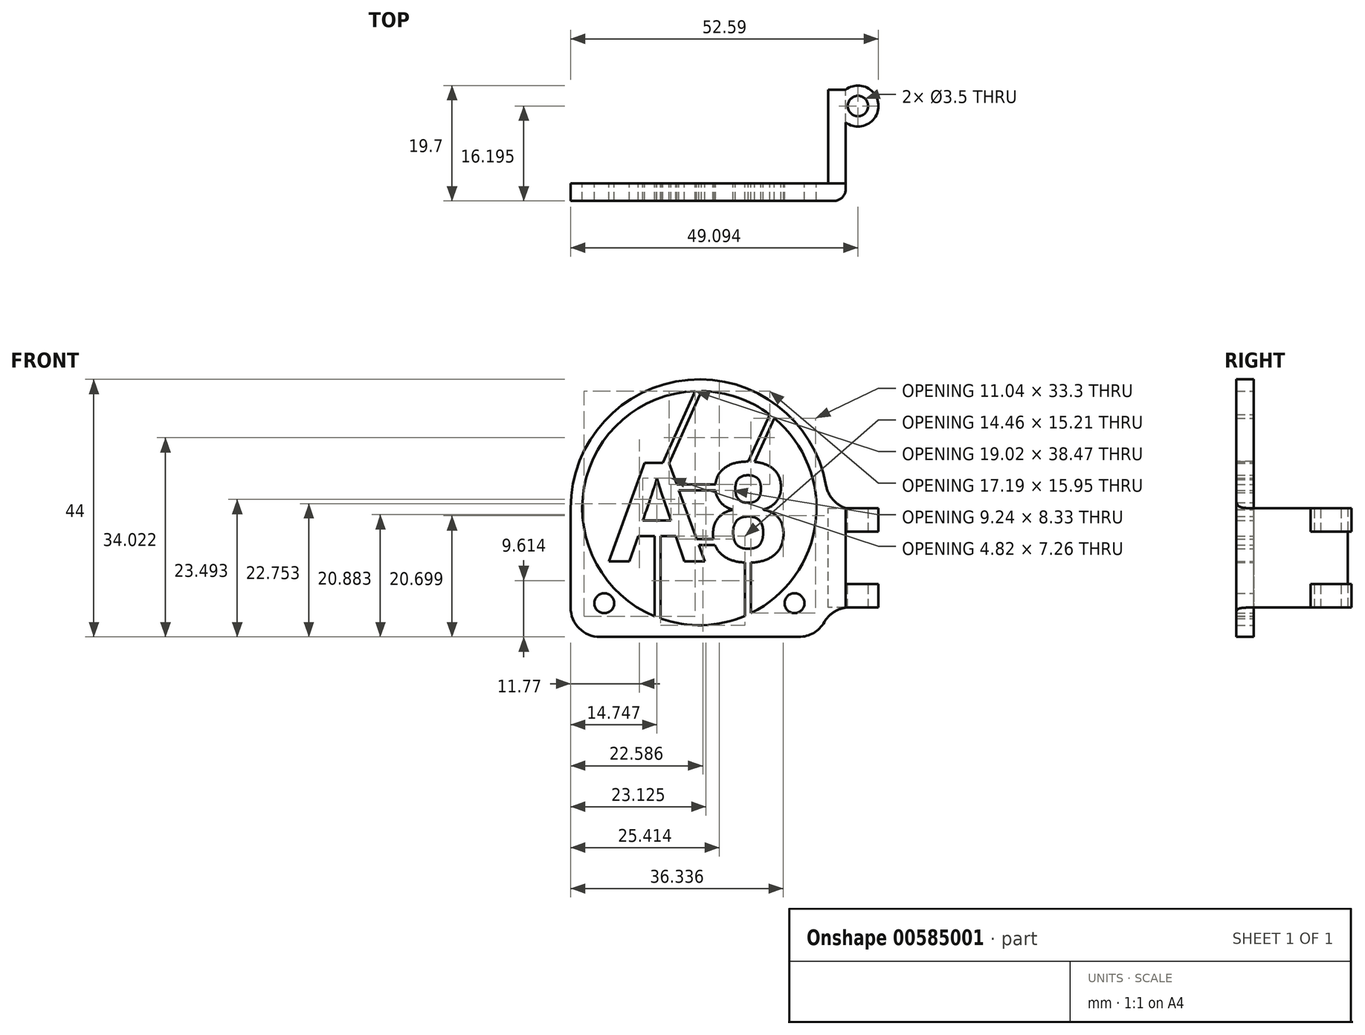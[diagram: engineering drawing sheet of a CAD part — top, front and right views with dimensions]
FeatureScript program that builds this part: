
annotation { "Feature Type Name" : "Feature", "Feature Type Description" : "" }
export const myFeature = defineFeature(function(context is Context, id is Id, definition is map)
    precondition{}
    {
        {
            var Q0;
            Q0=qCreatedBy(makeId("Front.planeOp"),FACE);
            var sketch = newSketch(context, id + "F0", { "sketchPlane" : qUnion([Q0])});
            skPoint(sketch, "E0.middle", {"position": v(0, 0) * mm});
            skCircle(sketch, "E1", {"center": v(-16.25, -16.25) * mm, "radius": 1.7 * mm});
            skCircle(sketch, "E2", {"center": v(16.25, -16.25) * mm, "radius": 1.7 * mm});
            skLineSegment(sketch, "E3.bottom", {"start": v(-17, -22) * mm, "end": v(17, -22) * mm});
            skLineSegment(sketch, "E3.left", {"start": v(-22, -17) * mm, "end": v(-22, 0) * mm});
            skLineSegment(sketch, "E3.right", {"start": v(22, -17) * mm, "end": v(22, 0) * mm});
            skCircle(sketch, "E4", {"center": v(0, 0) * mm, "radius": 20 * mm});
            skArc(sketch, "E5", {"start": v(22, 0) * mm, "mid": v(0, 22) * mm, "end": v(-22, 0) * mm});
            skPoint(sketch, "E6.orphan", {"position": v(-22, 22) * mm});
            skPoint(sketch, "E7.orphan", {"position": v(22, 22) * mm});
            skText(sketch, "E8", { "text": "A8", "fontName": "Arimo-Bold.ttf"});
            skLineSegment(sketch, "E9", {"start": v(-7.64, -3.72) * mm, "end": v(-7.64, -18.48) * mm});
            skLineSegment(sketch, "E10", {"start": v(-6.64, -18.86) * mm, "end": v(-6.64, -3.39) * mm});
            skLineSegment(sketch, "E11", {"start": v(7.81, -18.41) * mm, "end": v(7.81, -7.77) * mm});
            skLineSegment(sketch, "E12", {"start": v(8.81, -17.95) * mm, "end": v(8.81, -7.9) * mm});
            skLineSegment(sketch, "E13", {"start": v(3.64, -5.28) * mm, "end": v(-2.18, -5.28) * mm});
            skLineSegment(sketch, "E14", {"start": v(-2.25, -6.28) * mm, "end": v(3.9, -6.28) * mm});
            skLineSegment(sketch, "E15", {"start": v(3.52, 4.05) * mm, "end": v(-6.25, 4.05) * mm});
            skLineSegment(sketch, "E16", {"start": v(-5.4, 3.05) * mm, "end": v(4.44, 3.05) * mm});
            skLineSegment(sketch, "E17", {"start": v(-0.72, 19.99) * mm, "end": v(-6.99, 6.13) * mm});
            skLineSegment(sketch, "E18", {"start": v(12.01, 16) * mm, "end": v(8.12, 7.4) * mm});
            skLineSegment(sketch, "E19", {"start": v(12.82, 15.35) * mm, "end": v(9.09, 7.1) * mm});
            skLineSegment(sketch, "E20", {"start": v(0.38, 20) * mm, "end": v(-5.47, 7.07) * mm});
            skPoint(sketch, "E21.visualSharp", {"position": v(22, -22) * mm});
            skArc(sketch, "E21.filletArc", {"start": v(17, -22) * mm, "mid": v(20.54, -20.54) * mm, "end": v(22, -17) * mm});
            skPoint(sketch, "E22.visualSharp", {"position": v(-22, -22) * mm});
            skArc(sketch, "E22.filletArc", {"start": v(-22, -17) * mm, "mid": v(-20.54, -20.54) * mm, "end": v(-17, -22) * mm});
            const initialGuessF0  = {"E8": [-0.01606, -0.00907, 1, 0, 0.01756]};
            skSetInitialGuess(sketch, initialGuessF0);
            skSolve(sketch);
        }
        {
            var Q0;
            Q0=makeQuery(id+"F0.imprint","IMPRINT",FACE,{"disambiguationData":[TD([[makeQuery(id+"F0.imprint","IMPRINT",EDGE,{"derivedFrom":sQuery(id+"F0.wireOp",EDGE,"E1")}),-1.0]])]});
            var Q1;
            {var subQ18=sQuery(id+"F0.wireOp",EDGE,"E8.sketch_text.stroke-15");Q1=makeQuery(id+"F0.imprint","IMPRINT",FACE,{"disambiguationData":[TD([[makeQuery(id+"F0.imprint","IMPRINT",EDGE,{"derivedFrom":subQ18}),-1.0]])]});}
            var Q2;
            {var subQ3=sQuery(id+"F0.wireOp",EDGE,"E18");var subQ5=sQuery(id+"F0.wireOp",EDGE,"E4");var subQ6=makeQuery(id+"F0.imprint","INTERSECT",VERTEX,{"derivedFrom":[subQ5,subQ3]});Q2=makeQuery(id+"F0.imprint","IMPRINT",FACE,{"disambiguationData":[TD([[makeQuery(id+"F0.imprint","IMPRINT",EDGE,{"disambiguationData":[TD([[subQ6,1.0]])],"derivedFrom":subQ5}),1.0]])]});}
            var Q3;
            {var subQ0=sQuery(id+"F0.wireOp",EDGE,"E17");var subQ1=sQuery(id+"F0.wireOp",EDGE,"E4");var subQ2=makeQuery(id+"F0.imprint","INTERSECT",VERTEX,{"derivedFrom":[subQ1,subQ0]});Q3=makeQuery(id+"F0.imprint","IMPRINT",FACE,{"disambiguationData":[TD([[makeQuery(id+"F0.imprint","IMPRINT",EDGE,{"disambiguationData":[TD([[subQ2,1.0]])],"derivedFrom":subQ1}),1.0]])]});}
            var Q4;
            {var subQ11=sQuery(id+"F0.wireOp",EDGE,"E8.sketch_text.stroke-0");Q4=makeQuery(id+"F0.imprint","IMPRINT",FACE,{"disambiguationData":[TD([[makeQuery(id+"F0.imprint","IMPRINT",EDGE,{"derivedFrom":subQ11}),-1.0]])]});}
            var Q5;
            {var subQ0=sQuery(id+"F0.wireOp",EDGE,"E15");var subQ1=sQuery(id+"F0.wireOp",EDGE,"E8.sketch_text.stroke-6");var subQ2=makeQuery(id+"F0.imprint","INTERSECT",VERTEX,{"derivedFrom":[subQ1,subQ0]});Q5=makeQuery(id+"F0.imprint","IMPRINT",FACE,{"disambiguationData":[TD([[makeQuery(id+"F0.imprint","IMPRINT",EDGE,{"disambiguationData":[TD([[subQ2,-1.0]])],"derivedFrom":subQ1}),1.0]])]});}
            var Q6;
            {var subQ0=sQuery(id+"F0.wireOp",EDGE,"E13");var subQ1=sQuery(id+"F0.wireOp",EDGE,"E8.sketch_text.stroke-6");var subQ2=makeQuery(id+"F0.imprint","INTERSECT",VERTEX,{"derivedFrom":[subQ1,subQ0]});Q6=makeQuery(id+"F0.imprint","IMPRINT",FACE,{"disambiguationData":[TD([[makeQuery(id+"F0.imprint","IMPRINT",EDGE,{"disambiguationData":[TD([[subQ2,-1.0]])],"derivedFrom":subQ1}),1.0]])]});}
            var Q7;
            {var subQ0=sQuery(id+"F0.wireOp",EDGE,"E9");var subQ1=sQuery(id+"F0.wireOp",EDGE,"E4");var subQ2=makeQuery(id+"F0.imprint","INTERSECT",VERTEX,{"derivedFrom":[subQ1,subQ0]});Q7=makeQuery(id+"F0.imprint","IMPRINT",FACE,{"disambiguationData":[TD([[makeQuery(id+"F0.imprint","IMPRINT",EDGE,{"disambiguationData":[TD([[subQ2,-1.0]])],"derivedFrom":subQ1}),1.0]])]});}
            var Q8;
            {var subQ0=sQuery(id+"F0.wireOp",EDGE,"E11");var subQ1=sQuery(id+"F0.wireOp",EDGE,"E4");var subQ2=makeQuery(id+"F0.imprint","INTERSECT",VERTEX,{"derivedFrom":[subQ1,subQ0]});Q8=makeQuery(id+"F0.imprint","IMPRINT",FACE,{"disambiguationData":[TD([[makeQuery(id+"F0.imprint","IMPRINT",EDGE,{"disambiguationData":[TD([[subQ2,-1.0]])],"derivedFrom":subQ1}),1.0]])]});}
            extrude(context, id + "F1", {"entities" : qUnion([Q0, Q1, Q2, Q3, Q4, Q5, Q6, Q7, Q8]), "depth" : 3 * mm, "offsetDistance" : 25 * mm});
        }
        {
            var Q0;
            Q0=makeQuery(id+"F1.opExtrude","SWEPT_FACE",FACE,{"disambiguationData":[OSD([sQuery(id+"F0.wireOp",EDGE,"E3.right")])]});
            var sketch = newSketch(context, id + "F2", { "sketchPlane" : qUnion([Q0])});
            skLineSegment(sketch, "E23.bottom", {"start": v(-3, 0) * mm, "end": v(16, 0) * mm});
            skLineSegment(sketch, "E23.top", {"start": v(-3, -17) * mm, "end": v(16, -17) * mm});
            skLineSegment(sketch, "E23.left", {"start": v(-3, 0) * mm, "end": v(-3, -17) * mm});
            skLineSegment(sketch, "E23.right", {"start": v(16, 0) * mm, "end": v(16, -17) * mm});
            skSolve(sketch);
        }
        {
            var Q0;
            Q0 = qSketchRegion(id + "F2", true);
            extrude(context, id + "F3", {"entities" : qUnion([Q0]), "operationType" : NewBodyOperationType.ADD, "depth" : 3 * mm, "offsetDistance" : 25 * mm});
        }
        {
            var Q0;
            Q0=makeQuery(id+"F3.boolean.opBoolean","MERGE",EDGE,{"derivedFrom":[makeQuery(id+"F1.opExtrude","SWEPT_EDGE",EDGE,{"disambiguationData":[OSD([sQuery(id+"F0.wireOp",EDGE,"E3.right"),sQuery(id+"F0.wireOp",EDGE,"E21.filletArc")])]}),makeQuery(id+"F3.opExtrude","CAP_EDGE",EDGE,{"disambiguationData":[OSD([sQuery(id+"F2.wireOp",EDGE,"E23.top")])],"isStart":true})]});
            var Q1;
            Q1=makeQuery(id+"F3.boolean.opBoolean","MERGE",EDGE,{"derivedFrom":[makeQuery(id+"F1.opExtrude","SWEPT_EDGE",EDGE,{"disambiguationData":[OSD([sQuery(id+"F0.wireOp",EDGE,"E3.right"),sQuery(id+"F0.wireOp",EDGE,"E5")])]}),makeQuery(id+"F3.opExtrude","CAP_EDGE",EDGE,{"disambiguationData":[OSD([sQuery(id+"F2.wireOp",EDGE,"E23.bottom")])],"isStart":true})]});
            fillet(context, id + "F4", {"entities" : qUnion([Q0, Q1]), "radius" : 5 * mm, "tangentPropagation" : true, "allowEdgeOverflow" : false});
        }
        {
            var Q0;
            Q0=makeQuery(id+"F3.opExtrude","SWEPT_FACE",FACE,{"disambiguationData":[OSD([sQuery(id+"F2.wireOp",EDGE,"E23.bottom")])]});
            var sketch = newSketch(context, id + "F5", { "sketchPlane" : qUnion([Q0])});
            skCircle(sketch, "E24", {"center": v(27.1, 13.2) * mm, "radius": 1.75 * mm});
            skArc(sketch, "E25", {"start": v(25, 10.4) * mm, "mid": v(30.6, 13.2) * mm, "end": v(25, 16) * mm});
            skLineSegment(sketch, "E26", {"start": v(25, 16) * mm, "end": v(25, 10.4) * mm});
            skSolve(sketch);
        }
        {
            var Q0;
            Q0=makeQuery(id+"F5.imprint","IMPRINT",FACE,{"disambiguationData":[TD([[makeQuery(id+"F5.imprint","IMPRINT",EDGE,{"derivedFrom":sQuery(id+"F5.wireOp",EDGE,"E24")}),-1.0]])]});
            extrude(context, id + "F6", {"entities" : qUnion([Q0]), "operationType" : NewBodyOperationType.ADD, "oppositeDirection" : true, "depth" : 17 * mm, "offsetDistance" : 25 * mm});
        }
        {
            var Q0;
            Q0=makeQuery(id+"F3.opExtrude","CAP_FACE",FACE,{"disambiguationData":[OSD([sQuery(id+"F2.wireOp",EDGE,"E23.bottom"),sQuery(id+"F2.wireOp",EDGE,"E23.top"),sQuery(id+"F2.wireOp",EDGE,"E23.left"),sQuery(id+"F2.wireOp",EDGE,"E23.right")])],"isStart":false});
            var sketch = newSketch(context, id + "F7", { "sketchPlane" : qUnion([Q0])});
            skLineSegment(sketch, "E27", {"start": v(-3, 0) * mm, "end": v(16, -17) * mm, "construction": true});
            skLineSegment(sketch, "E28", {"start": v(16, 0) * mm, "end": v(-3, -17) * mm, "construction": true});
            skLineSegment(sketch, "E29.bottom", {"start": v(-3, -13) * mm, "end": v(16, -13) * mm});
            skLineSegment(sketch, "E29.top", {"start": v(-3, -4) * mm, "end": v(16, -4) * mm});
            skLineSegment(sketch, "E29.left", {"start": v(-3, -13) * mm, "end": v(-3, -4) * mm});
            skPoint(sketch, "E29.middle", {"position": v(6.5, -8.5) * mm});
            skLineSegment(sketch, "E30", {"start": v(-3, -4) * mm, "end": v(19.2, -4) * mm});
            skLineSegment(sketch, "E31", {"start": v(19.2, -4) * mm, "end": v(19.2, -13) * mm});
            skLineSegment(sketch, "E32", {"start": v(19.2, -13) * mm, "end": v(-3, -13) * mm});
            skSolve(sketch);
        }
        {
            var Q0;
            {var subQ0=sQuery(id+"F7.wireOp",EDGE,"E31");Q0=makeQuery(id+"F7.imprint","IMPRINT",FACE,{"disambiguationData":[TD([[makeQuery(id+"F7.imprint","IMPRINT",EDGE,{"derivedFrom":subQ0}),-1.0]])]});}
            var Q1;
            {var subQ0=sQuery(id+"F7.wireOp",EDGE,"E29.left");Q1=makeQuery(id+"F7.imprint","IMPRINT",FACE,{"disambiguationData":[TD([[makeQuery(id+"F7.imprint","IMPRINT",EDGE,{"derivedFrom":subQ0}),-1.0]])]});}
            extrude(context, id + "F8", {"entities" : qUnion([Q0, Q1]), "operationType" : NewBodyOperationType.REMOVE, "depth" : 25 * mm, "offsetDistance" : 25 * mm});
        }
        {
            var Q0;
            Q0=makeQuery(id+"F3.opExtrude","CAP_EDGE",EDGE,{"disambiguationData":[OSD([sQuery(id+"F2.wireOp",EDGE,"E23.left")])],"isStart":false});
            fillet(context, id + "F9", {"entities" : qUnion([Q0]), "radius" : 2 * mm, "tangentPropagation" : true, "allowEdgeOverflow" : false});
        }
    });
